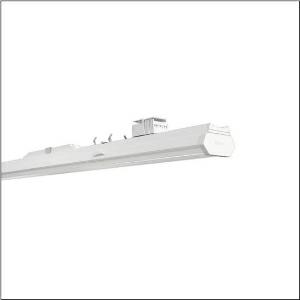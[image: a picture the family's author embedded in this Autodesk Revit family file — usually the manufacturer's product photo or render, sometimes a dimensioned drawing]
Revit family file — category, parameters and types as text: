
# Revit family: licross_21_protected_ho_52tp12dn4axm
name_source: partatom
category: Lighting Fixtures
units: mm (PartAtom-declared; Revit-internal decimal feet)

## family parameters
Cut with Voids When Loaded = No
Host = Face
Light Source = No
Part Type = Normal
Room Calculation Point = No
Round Connector Dimension = Use Diameter
Shared = No

## types (1)
- --- (1 x LED, 10000 lm, 56 W, 4000K)
    Apparent Load = 56 VA
    CIE Flux Codes = 70 91 97 98 100
    Color Rendering = 80
    Color Temperature = 4000K
    Default Elevation = 1800 mm
    Description = Licross 21 Protected HO, luminaire insert, of sheet steel, galvanised, coil coated, white, length: 1.500mm, width: 90mm, height: 103mm, LED rated luminous flux: 10.000lm, light colour: 840, SDCM (Standard Deviation of Colour Matching)MacAdam ≤ 3 SDCM (initial), control gear: DALI 2, with plug, 5-pole, with phase selection, mains connection: 220..240V, AC, 50/60Hz, rated input power: 56W, internal wiring halogen-free, primary light control with lens, of plastic, primary optical cover: cover, of PMMA, light emission: direct distribution, primary light characteristic: symmetric, protection rating (complete): IP64, insulation class (complete): insulation class I (protective earthing), certification: CE, ENEC, VDE, UKCA, protection symbol: D if used in an environment with conductive dust loads with corresponding accessories, impact resistance: IK06, permissible ambient temperature for indoor applications: -25..+45°C, corresponds to IFS (International Featured Standards) requirements for safety and quality in the food industry, reducing of maximum allowable ambient temperature of 5°C with ceiling mounting, LABS conformity tested according to VDMA 24364:2018-05, The light source and the operating device comply with the requirements of the Ecodesign Regulation (EU) 2019/2020 and are replaceable in accordance with this regulation, packaging unit: 1 piece
    Height = 92 mm
    Lamp = 1 x LED
    Lamp Light Flux = 10000 lm
    Lamp Power = 56 W
    Lamp count = 1
    Length = 1500 mm
    Luminous efficacy = 179 lm/W
    Manufacturer = Siteco
    ModVariant = No
    Model = 52TP12DN4AXM
    Mounting Place = Ceiling
    Mounting Type = Pendant
    Number of Poles = 1
    OnlyDefault = Yes
    Power Factor = 1
    Product Name = Licross 21 Protected HO
    Product group = luminaire insert | ceiling pendant
    ProductGroupID = 901
    Protection Class = Protection class I
    Protection Degree = IP 64
    RLX_Detail_Level = 1
    RLX_Emergency_Light_Flux = 0 lm
    RLX_Emergency_Type = 0
    RLX_Emergency_Type_DB = No
    RlxData = <blob elided: 24469 chars, md5=ee368f23>
    Socket = socket
    Standby Power = 0 W
    System Light Flux = 10000 lm
    System Power = 56 W
    Type Comments = factory setting: luminous flux: 100 % | dim-lin: 254 | 321 mA
    Type Image = l_1256148.jpg
    URL = http://relux.com
    VarID = @adj_129013
    Voltage = 0 V
    Weight = 0.00 kg
    Width = 88 mm

## geometry (parser evidence)
native form markers: Blend x4, Sweep x10
no freeform markers — native parametric forms only
